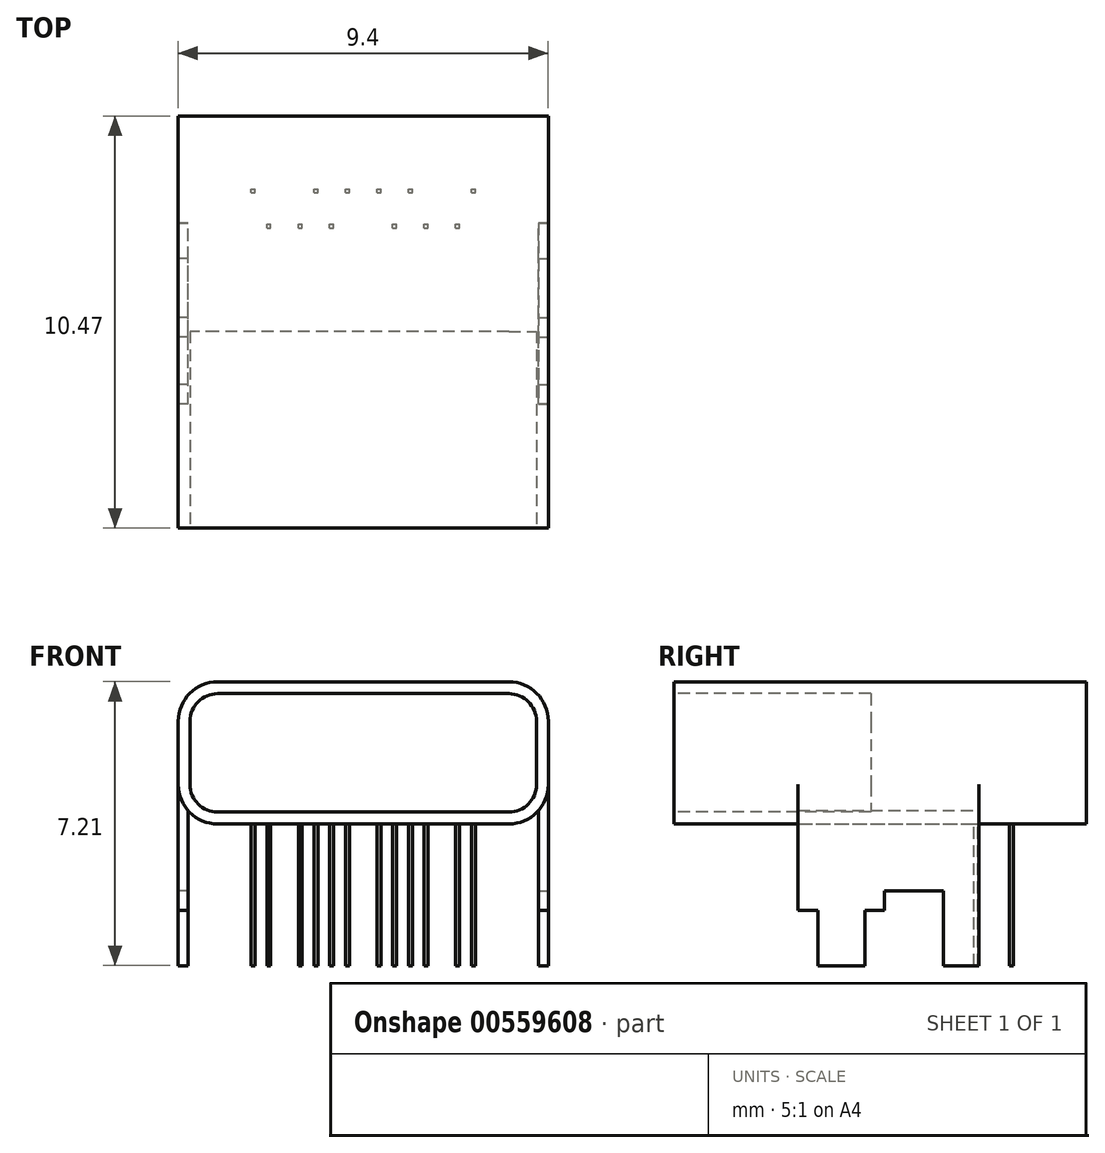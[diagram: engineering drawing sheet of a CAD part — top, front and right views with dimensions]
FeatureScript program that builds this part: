
annotation { "Feature Type Name" : "Feature", "Feature Type Description" : "" }
export const myFeature = defineFeature(function(context is Context, id is Id, definition is map)
    precondition{}
    {
        {
            var Q0;
            Q0=qCreatedBy(makeId("Front.planeOp"),FACE);
            var sketch = newSketch(context, id + "F0", { "sketchPlane" : qUnion([Q0])});
            skLineSegment(sketch, "E0.bottom", {"start": v(-5.06, 6.95) * mm, "end": v(4.34, 6.95) * mm});
            skLineSegment(sketch, "E0.top", {"start": v(-5.06, 3.34) * mm, "end": v(4.34, 3.34) * mm});
            skLineSegment(sketch, "E0.left", {"start": v(-5.06, 6.95) * mm, "end": v(-5.06, 3.34) * mm});
            skLineSegment(sketch, "E0.right", {"start": v(4.34, 6.95) * mm, "end": v(4.34, 3.34) * mm});
            skSolve(sketch);
        }
        {
            var Q0;
            Q0=makeQuery(id+"F0.imprint","IMPRINT",FACE,{"disambiguationData":[TD([[makeQuery(id+"F0.imprint","IMPRINT",EDGE,{"derivedFrom":sQuery(id+"F0.wireOp",EDGE,"E0.bottom")}),-1.0]])]});
            extrude(context, id + "F1", {"entities" : qUnion([Q0]), "depth" : 10.47 * mm, "offsetDistance" : 25 * mm});
        }
        {
            var Q0;
            Q0=makeQuery(id+"F1.opExtrude","SWEPT_EDGE",EDGE,{"disambiguationData":[OSD([sQuery(id+"F0.wireOp",EDGE,"E0.bottom"),sQuery(id+"F0.wireOp",EDGE,"E0.right")])]});
            var Q1;
            Q1=makeQuery(id+"F1.opExtrude","SWEPT_EDGE",EDGE,{"disambiguationData":[OSD([sQuery(id+"F0.wireOp",EDGE,"E0.top"),sQuery(id+"F0.wireOp",EDGE,"E0.right")])]});
            var Q2;
            Q2=makeQuery(id+"F1.opExtrude","SWEPT_EDGE",EDGE,{"disambiguationData":[OSD([sQuery(id+"F0.wireOp",EDGE,"E0.bottom"),sQuery(id+"F0.wireOp",EDGE,"E0.left")])]});
            var Q3;
            Q3=makeQuery(id+"F1.opExtrude","SWEPT_EDGE",EDGE,{"disambiguationData":[OSD([sQuery(id+"F0.wireOp",EDGE,"E0.top"),sQuery(id+"F0.wireOp",EDGE,"E0.left")])]});
            fillet(context, id + "F2", {"entities" : qUnion([Q0, Q1, Q2, Q3]), "radius" : 1 * mm, "tangentPropagation" : true, "allowEdgeOverflow" : false});
        }
        {
            var Q0;
            Q0=makeQuery(id+"F1.opExtrude","SWEPT_FACE",FACE,{"disambiguationData":[OSD([sQuery(id+"F0.wireOp",EDGE,"E0.right")])]});
            var sketch = newSketch(context, id + "F3", { "sketchPlane" : qUnion([Q0])});
            skLineSegment(sketch, "E1.0", {"start": v(0, 3.34) * mm, "end": v(-10.47, 3.34) * mm});
            skLineSegment(sketch, "E2.0", {"start": v(-10.47, 5.95) * mm, "end": v(-10.47, 4.34) * mm});
            skLineSegment(sketch, "E3.0", {"start": v(0, 5.95) * mm, "end": v(0, 4.34) * mm});
            skLineSegment(sketch, "E4.0", {"start": v(-10.47, 6.95) * mm, "end": v(0, 6.95) * mm});
            skLineSegment(sketch, "E5", {"start": v(-7.32, 1.14) * mm, "end": v(-6.82, 1.14) * mm});
            skLineSegment(sketch, "E6", {"start": v(-6.82, 1.14) * mm, "end": v(-6.82, -0.26) * mm});
            skLineSegment(sketch, "E7", {"start": v(-6.82, -0.26) * mm, "end": v(-5.62, -0.26) * mm});
            skLineSegment(sketch, "E8", {"start": v(-5.62, -0.26) * mm, "end": v(-5.62, 1.14) * mm});
            skLineSegment(sketch, "E9", {"start": v(-5.62, 1.14) * mm, "end": v(-5.12, 1.14) * mm});
            skLineSegment(sketch, "E10", {"start": v(-5.12, 1.14) * mm, "end": v(-5.12, 1.64) * mm});
            skLineSegment(sketch, "E11", {"start": v(-5.12, 1.64) * mm, "end": v(-3.62, 1.64) * mm});
            skLineSegment(sketch, "E12", {"start": v(-3.62, 1.64) * mm, "end": v(-3.62, -0.26) * mm});
            skLineSegment(sketch, "E13", {"start": v(-3.62, -0.26) * mm, "end": v(-2.72, -0.26) * mm});
            skLineSegment(sketch, "E14", {"start": v(-2.72, -0.26) * mm, "end": v(-2.72, 5.14) * mm});
            skLineSegment(sketch, "E15", {"start": v(-2.72, 5.14) * mm, "end": v(-7.32, 5.14) * mm});
            skLineSegment(sketch, "E16", {"start": v(-7.32, 1.14) * mm, "end": v(-7.32, 5.14) * mm});
            skPoint(sketch, "E17", {"position": v(-10.47, 5.14) * mm});
            skPoint(sketch, "E18", {"position": v(-6.22, -0.26) * mm});
            skPoint(sketch, "E19", {"position": v(-3.17, -0.26) * mm});
            skPoint(sketch, "E20", {"position": v(-5.02, 5.14) * mm});
            skPoint(sketch, "E21", {"position": v(-7.07, 1.14) * mm});
            skPoint(sketch, "E22", {"position": v(-5.37, 1.14) * mm});
            skSolve(sketch);
        }
        {
            var Q0;
            {var subQ6=sQuery(id+"F3.wireOp",EDGE,"E5");Q0=makeQuery(id+"F3.imprint","IMPRINT",FACE,{"disambiguationData":[TD([[makeQuery(id+"F3.imprint","IMPRINT",EDGE,{"derivedFrom":subQ6}),1.0]])]});}
            var Q1;
            {var subQ0=sQuery(id+"F3.wireOp",EDGE,"E14");var subQ1=sQuery(id+"F3.wireOp",EDGE,"E1.0");var subQ2=makeQuery(id+"F3.imprint","INTERSECT",VERTEX,{"derivedFrom":[subQ1,subQ0]});Q1=makeQuery(id+"F3.imprint","IMPRINT",FACE,{"disambiguationData":[TD([[makeQuery(id+"F3.imprint","IMPRINT",EDGE,{"disambiguationData":[TD([[subQ2,-1.0]])],"derivedFrom":subQ1}),-1.0]])]});}
            var Q2;
            {var subQ0=sQuery(id+"F3.wireOp",EDGE,"E15");Q2=makeQuery(id+"F3.imprint","IMPRINT",FACE,{"disambiguationData":[TD([[makeQuery(id+"F3.imprint","IMPRINT",EDGE,{"derivedFrom":subQ0}),1.0]])]});}
            extrude(context, id + "F4", {"entities" : qUnion([Q0, Q1, Q2]), "operationType" : NewBodyOperationType.ADD, "oppositeDirection" : true, "depth" : 0.25 * mm, "offsetDistance" : 25 * mm});
        }
        {
            var Q0;
            Q0=makeQuery(id+"F1.opExtrude","SWEPT_FACE",FACE,{"disambiguationData":[OSD([sQuery(id+"F0.wireOp",EDGE,"E0.left")])]});
            var sketch = newSketch(context, id + "F5", { "sketchPlane" : qUnion([Q0])});
            skLineSegment(sketch, "E23.0.0", {"start": v(10.47, 4.34) * mm, "end": v(7.32, 4.34) * mm});
            skLineSegment(sketch, "E23.0.1", {"start": v(7.32, 4.34) * mm, "end": v(7.32, 1.14) * mm});
            skLineSegment(sketch, "E23.0.2", {"start": v(7.32, 1.14) * mm, "end": v(6.82, 1.14) * mm});
            skLineSegment(sketch, "E23.0.3", {"start": v(6.82, 1.14) * mm, "end": v(6.82, -0.26) * mm});
            skLineSegment(sketch, "E23.0.4", {"start": v(6.82, -0.26) * mm, "end": v(5.62, -0.26) * mm});
            skLineSegment(sketch, "E23.0.5", {"start": v(5.62, -0.26) * mm, "end": v(5.62, 1.14) * mm});
            skLineSegment(sketch, "E23.0.6", {"start": v(5.62, 1.14) * mm, "end": v(5.12, 1.14) * mm});
            skLineSegment(sketch, "E23.0.7", {"start": v(5.12, 1.14) * mm, "end": v(5.12, 1.64) * mm});
            skLineSegment(sketch, "E23.0.8", {"start": v(5.12, 1.64) * mm, "end": v(3.62, 1.64) * mm});
            skLineSegment(sketch, "E23.0.9", {"start": v(3.62, 1.64) * mm, "end": v(3.62, -0.26) * mm});
            skLineSegment(sketch, "E23.0.10", {"start": v(3.62, -0.26) * mm, "end": v(2.72, -0.26) * mm});
            skLineSegment(sketch, "E23.0.11", {"start": v(2.72, -0.26) * mm, "end": v(2.72, 4.34) * mm});
            skLineSegment(sketch, "E23.0.12", {"start": v(2.72, 4.34) * mm, "end": v(0, 4.34) * mm});
            skLineSegment(sketch, "E23.0.13", {"start": v(0, 4.34) * mm, "end": v(0, 5.95) * mm});
            skLineSegment(sketch, "E23.0.14", {"start": v(0, 5.95) * mm, "end": v(10.47, 5.95) * mm});
            skLineSegment(sketch, "E23.0.15", {"start": v(10.47, 5.95) * mm, "end": v(10.47, 4.34) * mm});
            skSolve(sketch);
        }
        {
            var Q0;
            {var subQ0=sQuery(id+"F5.wireOp",EDGE,"E23.0.1");Q0=makeQuery(id+"F5.imprint","IMPRINT",FACE,{"disambiguationData":[TD([[makeQuery(id+"F5.imprint","IMPRINT",EDGE,{"derivedFrom":subQ0}),-1.0]])]});}
            extrude(context, id + "F6", {"entities" : qUnion([Q0]), "operationType" : NewBodyOperationType.ADD, "oppositeDirection" : true, "depth" : 0.25 * mm, "offsetDistance" : 25 * mm});
        }
        {
            var Q0;
            Q0=makeQuery(id+"F1.opExtrude","CAP_FACE",FACE,{"disambiguationData":[OSD([sQuery(id+"F0.wireOp",EDGE,"E0.bottom"),sQuery(id+"F0.wireOp",EDGE,"E0.top"),sQuery(id+"F0.wireOp",EDGE,"E0.left"),sQuery(id+"F0.wireOp",EDGE,"E0.right")])],"isStart":false});
            var sketch = newSketch(context, id + "F7", { "sketchPlane" : qUnion([Q0])});
            skLineSegment(sketch, "E24.0.0", {"start": v(-5.06, 5.95) * mm, "end": v(-5.06, 4.34) * mm});
            skArc(sketch, "E24.0.1", {"start": v(-5.06, 4.34) * mm, "mid": v(-4.76, 3.63) * mm, "end": v(-4.06, 3.34) * mm});
            skLineSegment(sketch, "E24.0.2", {"start": v(-4.06, 3.34) * mm, "end": v(3.34, 3.34) * mm});
            skArc(sketch, "E24.0.3", {"start": v(3.34, 3.34) * mm, "mid": v(4.05, 3.63) * mm, "end": v(4.34, 4.34) * mm});
            skLineSegment(sketch, "E24.0.4", {"start": v(4.34, 4.34) * mm, "end": v(4.34, 5.95) * mm});
            skArc(sketch, "E24.0.5", {"start": v(4.34, 5.95) * mm, "mid": v(4.05, 6.65) * mm, "end": v(3.34, 6.95) * mm});
            skLineSegment(sketch, "E24.0.6", {"start": v(3.34, 6.95) * mm, "end": v(-4.06, 6.95) * mm});
            skArc(sketch, "E24.0.7", {"start": v(-4.06, 6.95) * mm, "mid": v(-4.76, 6.65) * mm, "end": v(-5.06, 5.95) * mm});
            skArc(sketch, "E25.0", {"start": v(-4.06, 6.65) * mm, "mid": v(-4.55, 6.44) * mm, "end": v(-4.76, 5.95) * mm});
            skLineSegment(sketch, "E25.1", {"start": v(3.34, 6.65) * mm, "end": v(-4.06, 6.65) * mm});
            skLineSegment(sketch, "E25.2", {"start": v(-4.76, 5.95) * mm, "end": v(-4.76, 4.34) * mm});
            skArc(sketch, "E25.3", {"start": v(4.04, 5.95) * mm, "mid": v(3.84, 6.44) * mm, "end": v(3.34, 6.65) * mm});
            skArc(sketch, "E25.4", {"start": v(-4.76, 4.34) * mm, "mid": v(-4.55, 3.84) * mm, "end": v(-4.06, 3.64) * mm});
            skLineSegment(sketch, "E25.5", {"start": v(-4.06, 3.64) * mm, "end": v(3.34, 3.64) * mm});
            skArc(sketch, "E25.6", {"start": v(3.34, 3.64) * mm, "mid": v(3.84, 3.84) * mm, "end": v(4.04, 4.34) * mm});
            skLineSegment(sketch, "E25.7", {"start": v(4.04, 4.34) * mm, "end": v(4.04, 5.95) * mm});
            skSolve(sketch);
        }
        {
            var Q0;
            Q0=makeQuery(id+"F7.imprint","IMPRINT",FACE,{"disambiguationData":[TD([[makeQuery(id+"F7.imprint","IMPRINT",EDGE,{"derivedFrom":sQuery(id+"F7.wireOp",EDGE,"E25.0")}),1.0]])]});
            extrude(context, id + "F8", {"entities" : qUnion([Q0]), "operationType" : NewBodyOperationType.REMOVE, "oppositeDirection" : true, "depth" : 5 * mm, "offsetDistance" : 25 * mm});
        }
        {
            var Q0;
            Q0=makeQuery(id+"F1.opExtrude","SWEPT_FACE",FACE,{"disambiguationData":[OSD([sQuery(id+"F0.wireOp",EDGE,"E0.top")])]});
            var sketch = newSketch(context, id + "F9", { "sketchPlane" : qUnion([Q0])});
            skLineSegment(sketch, "E26.bottom", {"start": v(-2.8, 2.85) * mm, "end": v(-2.7, 2.85) * mm});
            skLineSegment(sketch, "E26.top", {"start": v(-2.8, 2.75) * mm, "end": v(-2.7, 2.75) * mm});
            skLineSegment(sketch, "E26.left", {"start": v(-2.8, 2.85) * mm, "end": v(-2.8, 2.75) * mm});
            skLineSegment(sketch, "E26.right", {"start": v(-2.7, 2.85) * mm, "end": v(-2.7, 2.75) * mm});
            skPoint(sketch, "E27", {"position": v(-2.76, 2.85) * mm});
            skPoint(sketch, "E28", {"position": v(-2.7, 2.8) * mm});
            skPoint(sketch, "E29", {"position": v(-2.76, 2.75) * mm});
            skPoint(sketch, "E30", {"position": v(-2.8, 2.8) * mm});
            skLineSegment(sketch, "E31.bottom", {"start": v(-2, 2.85) * mm, "end": v(-1.9, 2.85) * mm});
            skLineSegment(sketch, "E31.top", {"start": v(-2, 2.75) * mm, "end": v(-1.9, 2.75) * mm});
            skLineSegment(sketch, "E31.left", {"start": v(-2, 2.85) * mm, "end": v(-2, 2.75) * mm});
            skLineSegment(sketch, "E31.right", {"start": v(-1.9, 2.85) * mm, "end": v(-1.9, 2.75) * mm});
            skPoint(sketch, "E32", {"position": v(-1.96, 2.85) * mm});
            skPoint(sketch, "E33", {"position": v(-1.9, 2.8) * mm});
            skPoint(sketch, "E34", {"position": v(-1.96, 2.75) * mm});
            skPoint(sketch, "E35", {"position": v(-2, 2.8) * mm});
            skLineSegment(sketch, "E36.bottom", {"start": v(-1.2, 2.85) * mm, "end": v(-1.1, 2.85) * mm});
            skLineSegment(sketch, "E36.top", {"start": v(-1.2, 2.75) * mm, "end": v(-1.1, 2.75) * mm});
            skLineSegment(sketch, "E36.left", {"start": v(-1.2, 2.85) * mm, "end": v(-1.2, 2.75) * mm});
            skLineSegment(sketch, "E36.right", {"start": v(-1.1, 2.85) * mm, "end": v(-1.1, 2.75) * mm});
            skPoint(sketch, "E37", {"position": v(-1.16, 2.85) * mm});
            skPoint(sketch, "E38", {"position": v(-1.1, 2.8) * mm});
            skPoint(sketch, "E39", {"position": v(-1.16, 2.75) * mm});
            skPoint(sketch, "E40", {"position": v(-1.2, 2.8) * mm});
            skLineSegment(sketch, "E41.bottom", {"start": v(1.2, 2.85) * mm, "end": v(1.3, 2.85) * mm});
            skLineSegment(sketch, "E41.top", {"start": v(1.2, 2.75) * mm, "end": v(1.3, 2.75) * mm});
            skLineSegment(sketch, "E41.left", {"start": v(1.2, 2.85) * mm, "end": v(1.2, 2.75) * mm});
            skLineSegment(sketch, "E41.right", {"start": v(1.3, 2.85) * mm, "end": v(1.3, 2.75) * mm});
            skPoint(sketch, "E42", {"position": v(1.24, 2.85) * mm});
            skPoint(sketch, "E43", {"position": v(1.3, 2.8) * mm});
            skPoint(sketch, "E44", {"position": v(1.24, 2.75) * mm});
            skPoint(sketch, "E45", {"position": v(1.2, 2.8) * mm});
            skLineSegment(sketch, "E46.bottom", {"start": v(0.4, 2.85) * mm, "end": v(0.5, 2.85) * mm});
            skLineSegment(sketch, "E46.top", {"start": v(0.4, 2.75) * mm, "end": v(0.5, 2.75) * mm});
            skLineSegment(sketch, "E46.left", {"start": v(0.4, 2.85) * mm, "end": v(0.4, 2.75) * mm});
            skLineSegment(sketch, "E46.right", {"start": v(0.5, 2.85) * mm, "end": v(0.5, 2.75) * mm});
            skPoint(sketch, "E47", {"position": v(0.44, 2.85) * mm});
            skPoint(sketch, "E48", {"position": v(0.5, 2.8) * mm});
            skPoint(sketch, "E49", {"position": v(0.44, 2.75) * mm});
            skPoint(sketch, "E50", {"position": v(0.4, 2.8) * mm});
            skLineSegment(sketch, "E51.bottom", {"start": v(2, 2.85) * mm, "end": v(2.1, 2.85) * mm});
            skLineSegment(sketch, "E51.top", {"start": v(2, 2.75) * mm, "end": v(2.1, 2.75) * mm});
            skLineSegment(sketch, "E51.left", {"start": v(2, 2.85) * mm, "end": v(2, 2.75) * mm});
            skLineSegment(sketch, "E51.right", {"start": v(2.1, 2.85) * mm, "end": v(2.1, 2.75) * mm});
            skPoint(sketch, "E52", {"position": v(2.04, 2.85) * mm});
            skPoint(sketch, "E53", {"position": v(2.1, 2.8) * mm});
            skPoint(sketch, "E54", {"position": v(2.04, 2.75) * mm});
            skPoint(sketch, "E55", {"position": v(2, 2.8) * mm});
            skLineSegment(sketch, "E56", {"start": v(-1.1, 2.8) * mm, "end": v(0.4, 2.8) * mm});
            skPoint(sketch, "E57", {"position": v(-0.36, 2.8) * mm});
            skPoint(sketch, "E58.0", {"position": v(-0.36, 10.47) * mm});
            skLineSegment(sketch, "E59.bottom", {"start": v(-1.6, 1.95) * mm, "end": v(-1.5, 1.95) * mm});
            skLineSegment(sketch, "E59.top", {"start": v(-1.6, 1.85) * mm, "end": v(-1.5, 1.85) * mm});
            skLineSegment(sketch, "E59.left", {"start": v(-1.6, 1.95) * mm, "end": v(-1.6, 1.85) * mm});
            skLineSegment(sketch, "E59.right", {"start": v(-1.5, 1.95) * mm, "end": v(-1.5, 1.85) * mm});
            skPoint(sketch, "E60", {"position": v(-1.56, 1.95) * mm});
            skPoint(sketch, "E61", {"position": v(-1.5, 1.9) * mm});
            skPoint(sketch, "E62", {"position": v(-1.56, 1.85) * mm});
            skPoint(sketch, "E63", {"position": v(-1.6, 1.9) * mm});
            skLineSegment(sketch, "E64.bottom", {"start": v(-0.8, 1.95) * mm, "end": v(-0.7, 1.95) * mm});
            skLineSegment(sketch, "E64.top", {"start": v(-0.8, 1.85) * mm, "end": v(-0.7, 1.85) * mm});
            skLineSegment(sketch, "E64.left", {"start": v(-0.8, 1.95) * mm, "end": v(-0.8, 1.85) * mm});
            skLineSegment(sketch, "E64.right", {"start": v(-0.7, 1.95) * mm, "end": v(-0.7, 1.85) * mm});
            skPoint(sketch, "E65", {"position": v(-0.76, 1.95) * mm});
            skPoint(sketch, "E66", {"position": v(-0.7, 1.9) * mm});
            skPoint(sketch, "E67", {"position": v(-0.76, 1.85) * mm});
            skPoint(sketch, "E68", {"position": v(-0.8, 1.9) * mm});
            skLineSegment(sketch, "E69.bottom", {"start": v(0, 1.95) * mm, "end": v(0.1, 1.95) * mm});
            skLineSegment(sketch, "E69.top", {"start": v(0, 1.85) * mm, "end": v(0.1, 1.85) * mm});
            skLineSegment(sketch, "E69.left", {"start": v(0, 1.95) * mm, "end": v(0, 1.85) * mm});
            skLineSegment(sketch, "E69.right", {"start": v(0.1, 1.95) * mm, "end": v(0.1, 1.85) * mm});
            skPoint(sketch, "E70", {"position": v(0.04, 1.95) * mm});
            skPoint(sketch, "E71", {"position": v(0.1, 1.9) * mm});
            skPoint(sketch, "E72", {"position": v(0.04, 1.85) * mm});
            skPoint(sketch, "E73", {"position": v(0, 1.9) * mm});
            skLineSegment(sketch, "E74.bottom", {"start": v(0.8, 1.95) * mm, "end": v(0.9, 1.95) * mm});
            skLineSegment(sketch, "E74.top", {"start": v(0.8, 1.85) * mm, "end": v(0.9, 1.85) * mm});
            skLineSegment(sketch, "E74.left", {"start": v(0.8, 1.95) * mm, "end": v(0.8, 1.85) * mm});
            skLineSegment(sketch, "E74.right", {"start": v(0.9, 1.95) * mm, "end": v(0.9, 1.85) * mm});
            skPoint(sketch, "E75", {"position": v(0.84, 1.95) * mm});
            skPoint(sketch, "E76", {"position": v(0.9, 1.9) * mm});
            skPoint(sketch, "E77", {"position": v(0.84, 1.85) * mm});
            skPoint(sketch, "E78", {"position": v(0.8, 1.9) * mm});
            skLineSegment(sketch, "E79", {"start": v(-0.7, 1.9) * mm, "end": v(0, 1.9) * mm});
            skPoint(sketch, "E80", {"position": v(-0.36, 1.9) * mm});
            skLineSegment(sketch, "E81.bottom", {"start": v(2.4, 1.95) * mm, "end": v(2.5, 1.95) * mm});
            skLineSegment(sketch, "E81.top", {"start": v(2.4, 1.85) * mm, "end": v(2.5, 1.85) * mm});
            skLineSegment(sketch, "E81.left", {"start": v(2.4, 1.95) * mm, "end": v(2.4, 1.85) * mm});
            skLineSegment(sketch, "E81.right", {"start": v(2.5, 1.95) * mm, "end": v(2.5, 1.85) * mm});
            skPoint(sketch, "E82", {"position": v(2.44, 1.95) * mm});
            skPoint(sketch, "E83", {"position": v(2.5, 1.9) * mm});
            skPoint(sketch, "E84", {"position": v(2.44, 1.85) * mm});
            skPoint(sketch, "E85", {"position": v(2.4, 1.9) * mm});
            skLineSegment(sketch, "E86.bottom", {"start": v(-3.2, 1.95) * mm, "end": v(-3.1, 1.95) * mm});
            skLineSegment(sketch, "E86.top", {"start": v(-3.2, 1.85) * mm, "end": v(-3.1, 1.85) * mm});
            skLineSegment(sketch, "E86.left", {"start": v(-3.2, 1.95) * mm, "end": v(-3.2, 1.85) * mm});
            skLineSegment(sketch, "E86.right", {"start": v(-3.1, 1.95) * mm, "end": v(-3.1, 1.85) * mm});
            skPoint(sketch, "E87", {"position": v(-3.16, 1.95) * mm});
            skPoint(sketch, "E88", {"position": v(-3.1, 1.9) * mm});
            skPoint(sketch, "E89", {"position": v(-3.16, 1.85) * mm});
            skPoint(sketch, "E90", {"position": v(-3.2, 1.9) * mm});
            skSolve(sketch);
        }
        {
            var Q0;
            Q0=makeQuery(id+"F9.imprint","IMPRINT",FACE,{"disambiguationData":[TD([[makeQuery(id+"F9.imprint","IMPRINT",EDGE,{"derivedFrom":sQuery(id+"F9.wireOp",EDGE,"E86.bottom")}),-1.0]])]});
            var Q1;
            Q1=makeQuery(id+"F9.imprint","IMPRINT",FACE,{"disambiguationData":[TD([[makeQuery(id+"F9.imprint","IMPRINT",EDGE,{"derivedFrom":sQuery(id+"F9.wireOp",EDGE,"E59.bottom")}),-1.0]])]});
            var Q2;
            {var subQ1=sQuery(id+"F9.wireOp",EDGE,"E64.bottom");Q2=makeQuery(id+"F9.imprint","IMPRINT",FACE,{"disambiguationData":[TD([[makeQuery(id+"F9.imprint","IMPRINT",EDGE,{"derivedFrom":subQ1}),-1.0]])]});}
            var Q3;
            {var subQ3=sQuery(id+"F9.wireOp",EDGE,"E69.bottom");Q3=makeQuery(id+"F9.imprint","IMPRINT",FACE,{"disambiguationData":[TD([[makeQuery(id+"F9.imprint","IMPRINT",EDGE,{"derivedFrom":subQ3}),-1.0]])]});}
            var Q4;
            {var subQ1=sQuery(id+"F9.wireOp",EDGE,"E36.bottom");Q4=makeQuery(id+"F9.imprint","IMPRINT",FACE,{"disambiguationData":[TD([[makeQuery(id+"F9.imprint","IMPRINT",EDGE,{"derivedFrom":subQ1}),-1.0]])]});}
            var Q5;
            Q5=makeQuery(id+"F9.imprint","IMPRINT",FACE,{"disambiguationData":[TD([[makeQuery(id+"F9.imprint","IMPRINT",EDGE,{"derivedFrom":sQuery(id+"F9.wireOp",EDGE,"E31.bottom")}),-1.0]])]});
            var Q6;
            Q6=makeQuery(id+"F9.imprint","IMPRINT",FACE,{"disambiguationData":[TD([[makeQuery(id+"F9.imprint","IMPRINT",EDGE,{"derivedFrom":sQuery(id+"F9.wireOp",EDGE,"E26.bottom")}),-1.0]])]});
            var Q7;
            {var subQ3=sQuery(id+"F9.wireOp",EDGE,"E46.bottom");Q7=makeQuery(id+"F9.imprint","IMPRINT",FACE,{"disambiguationData":[TD([[makeQuery(id+"F9.imprint","IMPRINT",EDGE,{"derivedFrom":subQ3}),-1.0]])]});}
            var Q8;
            Q8=makeQuery(id+"F9.imprint","IMPRINT",FACE,{"disambiguationData":[TD([[makeQuery(id+"F9.imprint","IMPRINT",EDGE,{"derivedFrom":sQuery(id+"F9.wireOp",EDGE,"E74.bottom")}),-1.0]])]});
            var Q9;
            Q9=makeQuery(id+"F9.imprint","IMPRINT",FACE,{"disambiguationData":[TD([[makeQuery(id+"F9.imprint","IMPRINT",EDGE,{"derivedFrom":sQuery(id+"F9.wireOp",EDGE,"E41.bottom")}),-1.0]])]});
            var Q10;
            Q10=makeQuery(id+"F9.imprint","IMPRINT",FACE,{"disambiguationData":[TD([[makeQuery(id+"F9.imprint","IMPRINT",EDGE,{"derivedFrom":sQuery(id+"F9.wireOp",EDGE,"E51.bottom")}),-1.0]])]});
            var Q11;
            Q11=makeQuery(id+"F9.imprint","IMPRINT",FACE,{"disambiguationData":[TD([[makeQuery(id+"F9.imprint","IMPRINT",EDGE,{"derivedFrom":sQuery(id+"F9.wireOp",EDGE,"E81.bottom")}),-1.0]])]});
            var Q12;
            Q12=makeQuery(id+"F6.opExtrude","SWEPT_FACE",FACE,{"disambiguationData":[OSD([sQuery(id+"F5.wireOp",EDGE,"E23.0.4")])]});
            extrude(context, id + "F10", {"entities" : qUnion([Q0, Q1, Q2, Q3, Q4, Q5, Q6, Q7, Q8, Q9, Q10, Q11]), "operationType" : NewBodyOperationType.ADD, "endBound" : BoundingType.UP_TO_SURFACE, "depth" : 2 * mm, "endBoundEntityFace" : qUnion([Q12]), "offsetDistance" : 25 * mm});
        }
    });
